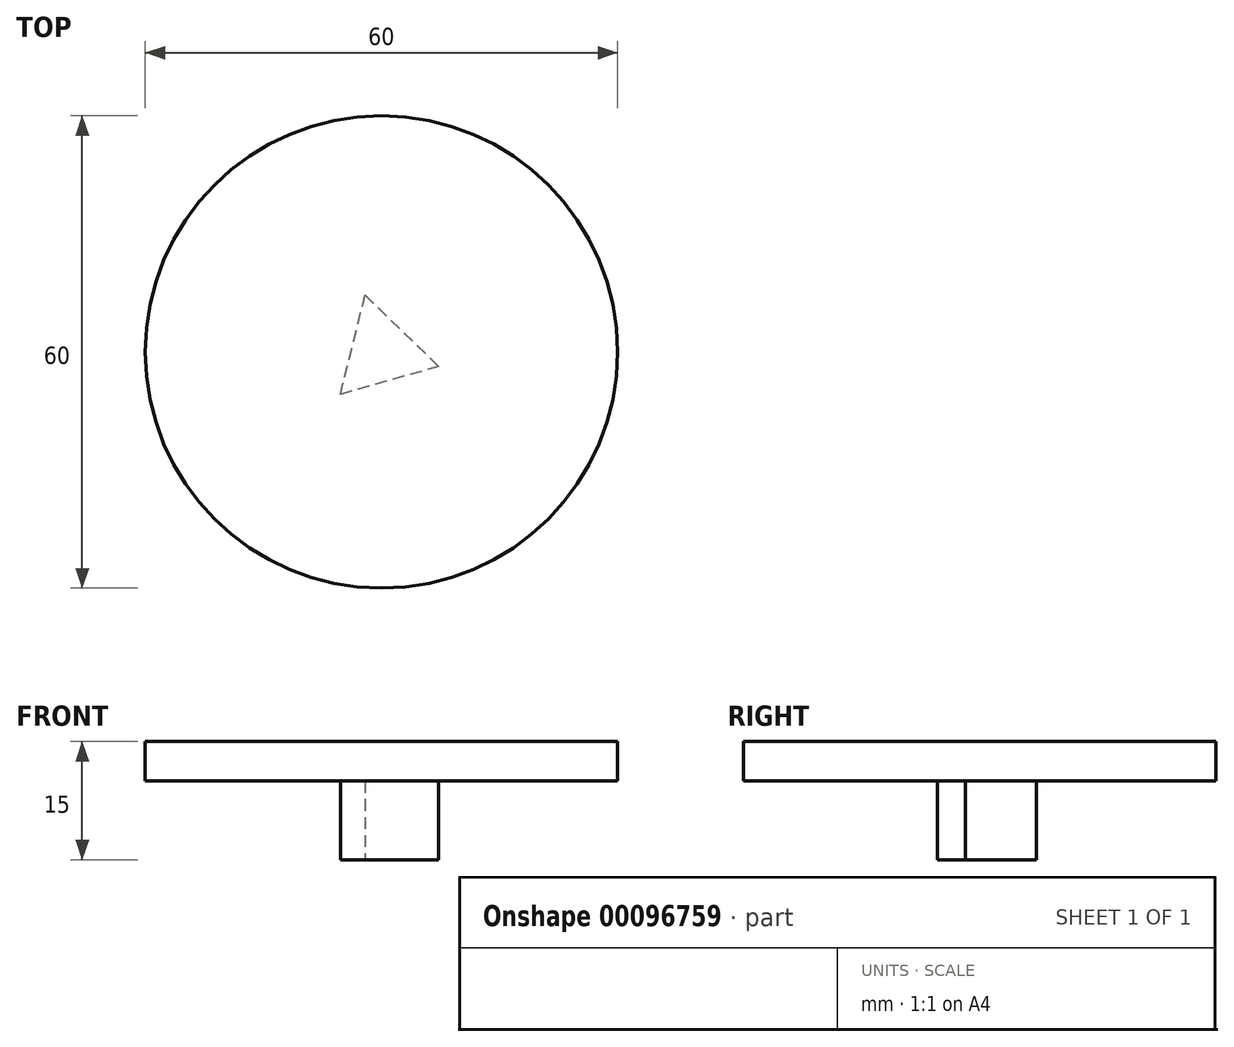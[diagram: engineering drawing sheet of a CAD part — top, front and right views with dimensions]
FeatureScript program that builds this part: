
annotation { "Feature Type Name" : "Feature", "Feature Type Description" : "" }
export const myFeature = defineFeature(function(context is Context, id is Id, definition is map)
    precondition{}
    {
        {
            var Q0;
            Q0=qCreatedBy(makeId("Top.planeOp"),FACE);
            var sketch = newSketch(context, id + "F0", { "sketchPlane" : qUnion([Q0])});
            skCircle(sketch, "E0.cCircle", {"center": v(0, 0) * mm, "radius": 7.5 * mm, "construction": true});
            skLineSegment(sketch, "E0.0", {"start": v(-5.22, -5.4) * mm, "end": v(-2.06, 7.22) * mm});
            skLineSegment(sketch, "E0.1", {"start": v(-2.06, 7.22) * mm, "end": v(7.28, -1.82) * mm});
            skLineSegment(sketch, "E0.2", {"start": v(7.28, -1.82) * mm, "end": v(-5.22, -5.4) * mm});
            skSolve(sketch);
        }
        {
            var Q0;
            Q0=qSketchRegion(id+"F0",true);
            extrude(context, id + "F1", {"entities" : qUnion([Q0]), "depth" : 10 * mm});
        }
        {
            var Q0;
            Q0=makeQuery(id+"F1.opExtrude","CAP_FACE",FACE,{"disambiguationData":[OSD([sQuery(id+"F0.wireOp",EDGE,"E0.0"),sQuery(id+"F0.wireOp",EDGE,"E0.1"),sQuery(id+"F0.wireOp",EDGE,"E0.2")])],"isStart":false});
            var sketch = newSketch(context, id + "F2", { "sketchPlane" : qUnion([Q0])});
            skCircle(sketch, "E1", {"center": v(0, 0) * mm, "radius": 30 * mm});
            skSolve(sketch);
        }
        {
            var Q0;
            Q0=qSketchRegion(id+"F2",true);
            extrude(context, id + "F3", {"entities" : qUnion([Q0]), "operationType" : NewBodyOperationType.ADD, "depth" : 5 * mm});
        }
    });
